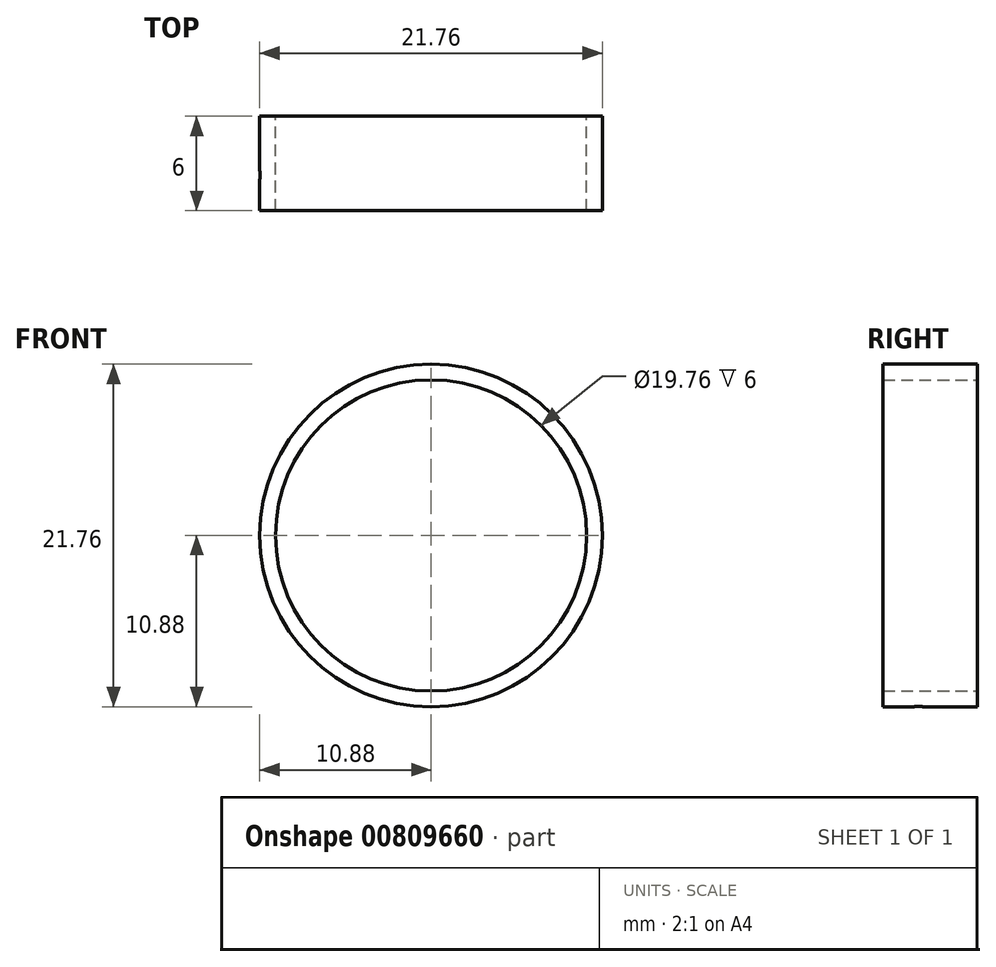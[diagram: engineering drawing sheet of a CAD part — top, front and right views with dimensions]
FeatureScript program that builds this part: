
annotation { "Feature Type Name" : "Feature", "Feature Type Description" : "" }
export const myFeature = defineFeature(function(context is Context, id is Id, definition is map)
    precondition{}
    {
        {
            var Q0;
            Q0=qCreatedBy(makeId("Front.planeOp"),FACE);
            var sketch = newSketch(context, id + "F0", { "sketchPlane" : qUnion([Q0])});
            skCircle(sketch, "E0", {"center": v(0, 0) * mm, "radius": 10.88 * mm});
            skSolve(sketch);
        }
        {
            var Q0;
            Q0 = qSketchRegion(id + "F0", true);
            extrude(context, id + "F1", {"entities" : qUnion([Q0]), "depth" : 6 * mm, "offsetDistance" : 25.4 * mm});
        }
        {
            var Q0;
            Q0=qCreatedBy(makeId("Front.planeOp"),FACE);
            var sketch = newSketch(context, id + "F2", { "sketchPlane" : qUnion([Q0])});
            skCircle(sketch, "E1", {"center": v(0, 0) * mm, "radius": 9.88 * mm});
            skSolve(sketch);
        }
        {
            var Q0;
            Q0=qCreatedBy(makeId("Front.planeOp"),FACE);
            cPlane(context, id + "F3", {"entities" : qUnion([Q0]), "cplaneType" : CPlaneType.OFFSET, "offset" : 4 * mm, "width" : 152.4 * mm, "height" : 152.4 * mm});
        }
        {
            var Q0;
            Q0=qCreatedBy(id+"F3.planeOp",FACE);
            var sketch = newSketch(context, id + "F4", { "sketchPlane" : qUnion([Q0])});
            skCircle(sketch, "E2", {"center": v(0, 0) * mm, "radius": 10.88 * mm});
            skSolve(sketch);
        }
        {
            var Q0;
            Q0 = qSketchRegion(id + "F4", true);
            extrude(context, id + "F5", {"entities" : qUnion([Q0]), "operationType" : NewBodyOperationType.REMOVE, "oppositeDirection" : true, "depth" : .5 * mm, "offsetDistance" : 25.4 * mm});
        }
        {
            var Q0;
            Q0=qCreatedBy(id+"F3.planeOp",FACE);
            var sketch = newSketch(context, id + "F6", { "sketchPlane" : qUnion([Q0])});
            skCircle(sketch, "E3", {"center": v(0, 0) * mm, "radius": 10.88 * mm});
            skSolve(sketch);
        }
        {
            var Q0;
            Q0 = qSketchRegion(id + "F6", true);
            extrude(context, id + "F7", {"entities" : qUnion([Q0]), "operationType" : NewBodyOperationType.ADD, "oppositeDirection" : true, "depth" : .5 * mm, "offsetDistance" : 25.4 * mm});
        }
        {
            var Q0;
            Q0 = qSketchRegion(id + "F2", true);
            extrude(context, id + "F8", {"entities" : qUnion([Q0]), "operationType" : NewBodyOperationType.REMOVE, "depth" : 25.4 * mm, "offsetDistance" : 25.4 * mm});
        }
    });
